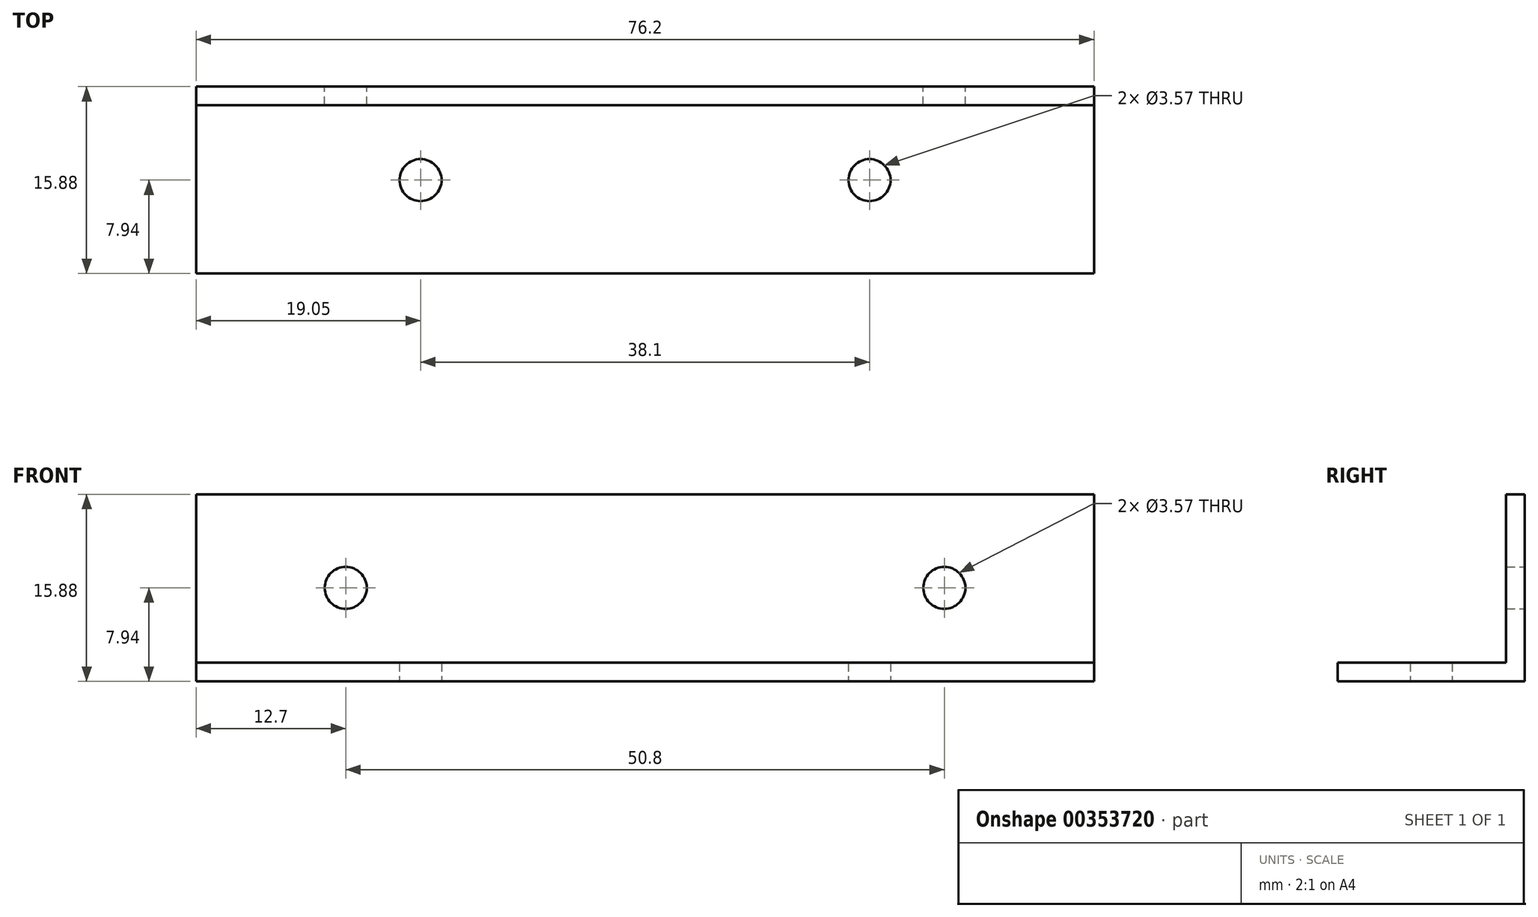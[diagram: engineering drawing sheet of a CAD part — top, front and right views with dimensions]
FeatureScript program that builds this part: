
annotation { "Feature Type Name" : "Feature", "Feature Type Description" : "" }
export const myFeature = defineFeature(function(context is Context, id is Id, definition is map)
    precondition{}
    {
        {
            var Q0;
            Q0=qCreatedBy(makeId("Front.planeOp"),FACE);
            var sketch = newSketch(context, id + "F0", { "sketchPlane" : qUnion([Q0])});
            skLineSegment(sketch, "E0.bottom", {"start": v(-38.1, 7.94) * mm, "end": v(38.1, 7.94) * mm});
            skLineSegment(sketch, "E0.top", {"start": v(-38.1, -7.94) * mm, "end": v(38.1, -7.94) * mm});
            skLineSegment(sketch, "E0.left", {"start": v(-38.1, 7.94) * mm, "end": v(-38.1, -7.94) * mm});
            skLineSegment(sketch, "E0.right", {"start": v(38.1, 7.94) * mm, "end": v(38.1, -7.94) * mm});
            skPoint(sketch, "E0.middle", {"position": v(0, 0) * mm});
            skSolve(sketch);
        }
        {
            var Q0;
            Q0 = qSketchRegion(id + "F0", true);
            extrude(context, id + "F1", {"entities" : qUnion([Q0]), "depth" : 15.88 * mm, "symmetric" : true});
        }
        {
            var Q0;
            Q0=makeQuery(id+"F1.opExtrude","CAP_FACE",FACE,{"disambiguationData":[OSD([sQuery(id+"F0.wireOp",EDGE,"E0.bottom"),sQuery(id+"F0.wireOp",EDGE,"E0.top"),sQuery(id+"F0.wireOp",EDGE,"E0.left"),sQuery(id+"F0.wireOp",EDGE,"E0.right")])],"isStart":false});
            var sketch = newSketch(context, id + "F2", { "sketchPlane" : qUnion([Q0])});
            skLineSegment(sketch, "E1", {"start": v(-38.1, -6.35) * mm, "end": v(38.1, -6.35) * mm, "construction": true});
            skLineSegment(sketch, "E2", {"start": v(38.1, -6.35) * mm, "end": v(38.1, -7.94) * mm, "construction": true});
            skLineSegment(sketch, "E3", {"start": v(38.1, -7.94) * mm, "end": v(-38.1, -7.94) * mm, "construction": true});
            skLineSegment(sketch, "E4", {"start": v(-38.1, -7.94) * mm, "end": v(-38.1, -6.35) * mm, "construction": true});
            skLineSegment(sketch, "E5", {"start": v(-38.1, -6.35) * mm, "end": v(-38.1, 7.94) * mm});
            skLineSegment(sketch, "E6", {"start": v(-38.1, 7.94) * mm, "end": v(38.1, 7.94) * mm});
            skLineSegment(sketch, "E7", {"start": v(38.1, 7.94) * mm, "end": v(38.1, -6.35) * mm});
            skLineSegment(sketch, "E8", {"start": v(-38.1, -6.35) * mm, "end": v(38.1, -6.35) * mm});
            skSolve(sketch);
        }
        {
            var Q0;
            Q0 = qSketchRegion(id + "F2", true);
            extrude(context, id + "F3", {"entities" : qUnion([Q0]), "operationType" : NewBodyOperationType.REMOVE, "oppositeDirection" : true, "depth" : 14.29 * mm});
        }
        {
            var Q0;
            Q0=makeQuery(id+"F3.boolean.opBoolean","COPY",FACE,{"derivedFrom":makeQuery(id+"F3.opExtrude","SWEPT_FACE",FACE,{"disambiguationData":[OSD([sQuery(id+"F2.wireOp",EDGE,"E8")])]})});
            var sketch = newSketch(context, id + "F4", { "sketchPlane" : qUnion([Q0])});
            skLineSegment(sketch, "E9", {"start": v(-38.1, 6.35) * mm, "end": v(-19.05, 6.35) * mm, "construction": true});
            skLineSegment(sketch, "E10", {"start": v(38.1, 6.35) * mm, "end": v(19.05, 6.35) * mm, "construction": true});
            skLineSegment(sketch, "E11", {"start": v(0, 0) * mm, "end": v(-38.1, 0) * mm, "construction": true});
            skLineSegment(sketch, "E12", {"start": v(-38.1, 0) * mm, "end": v(38.1, 0) * mm, "construction": true});
            skLineSegment(sketch, "E13", {"start": v(-19.05, 6.35) * mm, "end": v(-19.05, 0) * mm, "construction": true});
            skLineSegment(sketch, "E14", {"start": v(19.05, 6.35) * mm, "end": v(19.05, 0) * mm, "construction": true});
            skCircle(sketch, "E15", {"center": v(-19.05, 0) * mm, "radius": 1.79 * mm});
            skCircle(sketch, "E16", {"center": v(19.05, 0) * mm, "radius": 1.79 * mm});
            skSolve(sketch);
        }
        {
            var Q0;
            Q0 = qSketchRegion(id + "F4", true);
            extrude(context, id + "F5", {"entities" : qUnion([Q0]), "operationType" : NewBodyOperationType.REMOVE, "depth" : 25.4 * mm, "symmetric" : true});
        }
        {
            var Q0;
            Q0=makeQuery(id+"F3.boolean.opBoolean","COPY",FACE,{"derivedFrom":makeQuery(id+"F3.opExtrude","CAP_FACE",FACE,{"disambiguationData":[OSD([sQuery(id+"F2.wireOp",EDGE,"E5"),sQuery(id+"F2.wireOp",EDGE,"E6"),sQuery(id+"F2.wireOp",EDGE,"E7"),sQuery(id+"F2.wireOp",EDGE,"E8")])],"isStart":false})});
            var sketch = newSketch(context, id + "F6", { "sketchPlane" : qUnion([Q0])});
            skLineSegment(sketch, "E17", {"start": v(-38.1, 7.94) * mm, "end": v(-25.4, 7.94) * mm, "construction": true});
            skLineSegment(sketch, "E18", {"start": v(38.1, 7.94) * mm, "end": v(25.4, 7.94) * mm, "construction": true});
            skLineSegment(sketch, "E19", {"start": v(-38.1, 0) * mm, "end": v(38.1, 0) * mm, "construction": true});
            skPoint(sketch, "E19.startSnap0", {"position": v(-38.1, 0.8) * mm});
            skLineSegment(sketch, "E20", {"start": v(-25.4, 7.94) * mm, "end": v(-25.4, 0) * mm, "construction": true});
            skLineSegment(sketch, "E21", {"start": v(25.4, 7.94) * mm, "end": v(25.4, 0) * mm, "construction": true});
            skCircle(sketch, "E22", {"center": v(-25.4, 0) * mm, "radius": 1.79 * mm});
            skCircle(sketch, "E23", {"center": v(25.4, 0) * mm, "radius": 1.79 * mm});
            skSolve(sketch);
        }
        {
            var Q0;
            Q0 = qSketchRegion(id + "F6", true);
            extrude(context, id + "F7", {"entities" : qUnion([Q0]), "operationType" : NewBodyOperationType.REMOVE, "depth" : 25.4 * mm, "symmetric" : true});
        }
    });
